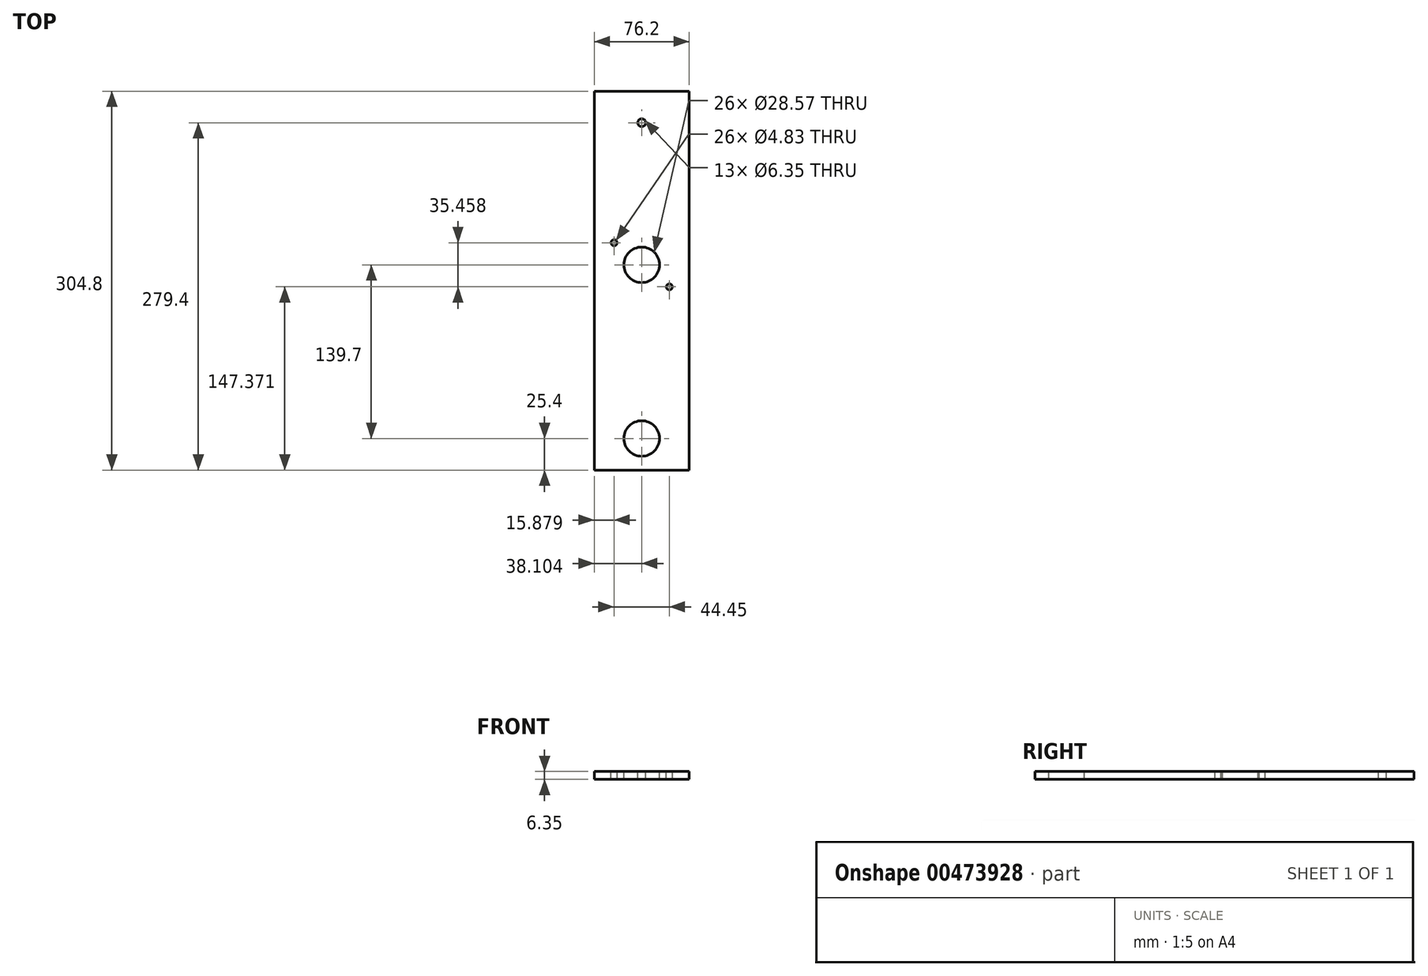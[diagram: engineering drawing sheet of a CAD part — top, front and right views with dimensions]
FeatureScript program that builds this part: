
annotation { "Feature Type Name" : "Feature", "Feature Type Description" : "" }
export const myFeature = defineFeature(function(context is Context, id is Id, definition is map)
    precondition{}
    {
        {
            var Q0;
            Q0=qCreatedBy(makeId("Top.planeOp"),FACE);
            var sketch = newSketch(context, id + "F0", { "sketchPlane" : qUnion([Q0])});
            skLineSegment(sketch, "E0.bottom", {"start": v(0.91, 165.02) * mm, "end": v(77.11, 165.02) * mm});
            skLineSegment(sketch, "E0.top", {"start": v(0.91, -139.78) * mm, "end": v(77.11, -139.78) * mm});
            skLineSegment(sketch, "E0.left", {"start": v(0.91, 165.02) * mm, "end": v(0.91, -139.78) * mm});
            skLineSegment(sketch, "E0.right", {"start": v(77.11, 165.02) * mm, "end": v(77.11, -139.78) * mm});
            skSolve(sketch);
        }
        {
            var Q0;
            Q0=makeQuery(id+"F0.imprint","IMPRINT",FACE,{"disambiguationData":[TD([[makeQuery(id+"F0.imprint","IMPRINT",EDGE,{"derivedFrom":sQuery(id+"F0.wireOp",EDGE,"E0.bottom")}),-1.0]])]});
            extrude(context, id + "F1", {"entities" : qUnion([Q0]), "depth" : 6.35 * mm});
        }
        {
            var Q0;
            Q0=makeQuery(id+"F1.opExtrude","CAP_FACE",FACE,{"disambiguationData":[OSD([sQuery(id+"F0.wireOp",EDGE,"E0.bottom"),sQuery(id+"F0.wireOp",EDGE,"E0.top"),sQuery(id+"F0.wireOp",EDGE,"E0.left"),sQuery(id+"F0.wireOp",EDGE,"E0.right")])],"isStart":false});
            var sketch = newSketch(context, id + "F2", { "sketchPlane" : qUnion([Q0])});
            skCircle(sketch, "E1", {"center": v(39.01, 139.62) * mm, "radius": 3.18 * mm});
            skSolve(sketch);
        }
        {
            var Q0;
            Q0=makeQuery(id+"F2.imprint","IMPRINT",FACE,{"disambiguationData":[TD([[makeQuery(id+"F2.imprint","IMPRINT",EDGE,{"derivedFrom":sQuery(id+"F2.wireOp",EDGE,"E1")}),1.0]])]});
            extrude(context, id + "F3", {"entities" : qUnion([Q0]), "operationType" : NewBodyOperationType.REMOVE, "oppositeDirection" : true, "depth" : 6.35 * mm});
        }
        {
            var Q0;
            Q0=makeQuery(id+"F1.opExtrude","CAP_FACE",FACE,{"disambiguationData":[OSD([sQuery(id+"F0.wireOp",EDGE,"E0.bottom"),sQuery(id+"F0.wireOp",EDGE,"E0.top"),sQuery(id+"F0.wireOp",EDGE,"E0.left"),sQuery(id+"F0.wireOp",EDGE,"E0.right")])],"isStart":false});
            var sketch = newSketch(context, id + "F4", { "sketchPlane" : qUnion([Q0])});
            skCircle(sketch, "E2", {"center": v(39.01, -114.38) * mm, "radius": 14.29 * mm});
            skSolve(sketch);
        }
        {
            var Q0;
            Q0=makeQuery(id+"F4.imprint","IMPRINT",FACE,{"disambiguationData":[TD([[makeQuery(id+"F4.imprint","IMPRINT",EDGE,{"derivedFrom":sQuery(id+"F4.wireOp",EDGE,"E2")}),1.0]])]});
            extrude(context, id + "F5", {"entities" : qUnion([Q0]), "operationType" : NewBodyOperationType.REMOVE, "oppositeDirection" : true, "depth" : 6.35 * mm});
        }
        {
            var Q0;
            Q0=makeQuery(id+"F1.opExtrude","CAP_FACE",FACE,{"disambiguationData":[OSD([sQuery(id+"F0.wireOp",EDGE,"E0.bottom"),sQuery(id+"F0.wireOp",EDGE,"E0.top"),sQuery(id+"F0.wireOp",EDGE,"E0.left"),sQuery(id+"F0.wireOp",EDGE,"E0.right")])],"isStart":false});
            var sketch = newSketch(context, id + "F6", { "sketchPlane" : qUnion([Q0])});
            skCircle(sketch, "E3", {"center": v(39.01, 25.32) * mm, "radius": 14.29 * mm});
            skSolve(sketch);
        }
        {
            var Q0;
            Q0=makeQuery(id+"F6.imprint","IMPRINT",FACE,{"disambiguationData":[TD([[makeQuery(id+"F6.imprint","IMPRINT",EDGE,{"derivedFrom":sQuery(id+"F6.wireOp",EDGE,"E3")}),1.0]])]});
            extrude(context, id + "F7", {"entities" : qUnion([Q0]), "operationType" : NewBodyOperationType.REMOVE, "oppositeDirection" : true, "depth" : 6.35 * mm});
        }
        {
            var Q0;
            Q0=makeQuery(id+"F1.opExtrude","CAP_FACE",FACE,{"disambiguationData":[OSD([sQuery(id+"F0.wireOp",EDGE,"E0.bottom"),sQuery(id+"F0.wireOp",EDGE,"E0.top"),sQuery(id+"F0.wireOp",EDGE,"E0.left"),sQuery(id+"F0.wireOp",EDGE,"E0.right")])],"isStart":false});
            var sketch = newSketch(context, id + "F8", { "sketchPlane" : qUnion([Q0])});
            skCircle(sketch, "E4", {"center": v(61.24, 7.6) * mm, "radius": 2.41 * mm});
            skSolve(sketch);
        }
        {
            var Q0;
            Q0=makeQuery(id+"F8.imprint","IMPRINT",FACE,{"disambiguationData":[TD([[makeQuery(id+"F8.imprint","IMPRINT",EDGE,{"derivedFrom":sQuery(id+"F8.wireOp",EDGE,"E4")}),-1.0]])]});
            var sketch = newSketch(context, id + "F9", { "sketchPlane" : qUnion([Q0])});
            skCircle(sketch, "E5", {"center": v(16.79, 43.05) * mm, "radius": 2.41 * mm});
            skSolve(sketch);
        }
        {
            var Q0;
            Q0 = qSketchRegion(id + "F8", true);
            extrude(context, id + "F10", {"entities" : qUnion([Q0]), "operationType" : NewBodyOperationType.REMOVE, "oppositeDirection" : true, "depth" : 6.35 * mm});
        }
        {
            var Q0;
            Q0 = qSketchRegion(id + "F9", true);
            extrude(context, id + "F11", {"entities" : qUnion([Q0]), "operationType" : NewBodyOperationType.REMOVE, "oppositeDirection" : true, "depth" : 6.35 * mm});
        }
    });
